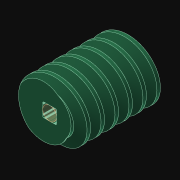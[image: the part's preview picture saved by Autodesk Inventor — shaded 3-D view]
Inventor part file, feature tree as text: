
AUTODESK INVENTOR PART (.ipt)
format: ipt  version: 2021.3 (Build 253353010, 353A)  size: 847,872 bytes
history: native  units: in
note: dims shown in document units (in); Inventor stores cm internally (conversion verified against a paired STEP export)
features: other x2, imported_body x1, sketch x1, extrude x1
ambient origin geometry x8: Origin, YZ Plane, XZ Plane, XY Plane, X Axis, Y Axis, Z Axis, Center Point
bodies: Body1 (feature_tree), Body2 (feature_tree)
feature tree (5):
  parser-record x1  (decoder bookkeeping rows leaked as tree rows — omitted from the tree; the rows remain in map.json)
  imported_body  "Base1"
  sketch  "Sketch1"  dims[d0=1.0in d1=0.0in]
  other  "Srf1"
  extrude  "ExtrusionSrf1"  [1 undecoded]
note: 1 required parameter value undecoded (feature->parameter linkage not recoverable at this tier; creation-order binding heuristic only, values carry confidence <= 0.55)
